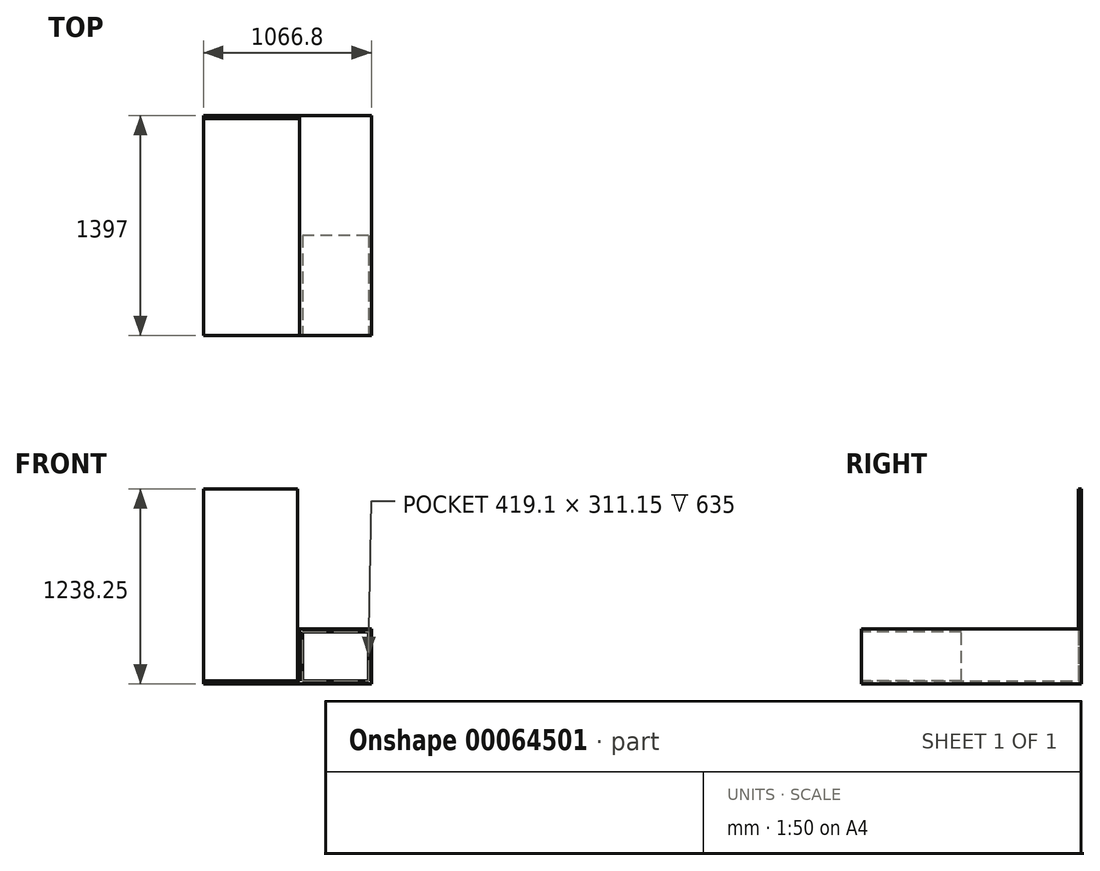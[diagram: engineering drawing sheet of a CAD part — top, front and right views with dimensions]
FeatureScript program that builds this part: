
annotation { "Feature Type Name" : "Feature", "Feature Type Description" : "" }
export const myFeature = defineFeature(function(context is Context, id is Id, definition is map)
    precondition{}
    {
        {
            var Q0;
            Q0=qCreatedBy(makeId("Top.planeOp"),FACE);
            var sketch = newSketch(context, id + "F0", { "sketchPlane" : qUnion([Q0])});
            skLineSegment(sketch, "E0.rect.bottom", {"start": v(533.4, -698.5) * mm, "end": v(-533.4, -698.5) * mm});
            skLineSegment(sketch, "E0.rect.top", {"start": v(533.4, 698.5) * mm, "end": v(-533.4, 698.5) * mm});
            skLineSegment(sketch, "E0.rect.left", {"start": v(533.4, -698.5) * mm, "end": v(533.4, 698.5) * mm});
            skLineSegment(sketch, "E0.rect.right", {"start": v(-533.4, -698.5) * mm, "end": v(-533.4, 698.5) * mm});
            skPoint(sketch, "E0.rect.middle", {"position": v(0, 0) * mm});
            skSolve(sketch);
        }
        {
            var Q0;
            Q0=makeQuery(id+"F0.imprint","IMPRINT",FACE,{"disambiguationData":[TD([[makeQuery(id+"F0.imprint","IMPRINT",EDGE,{"derivedFrom":sQuery(id+"F0.wireOp",EDGE,"E0.rect.bottom")}),-1.0]])]});
            extrude(context, id + "F1", {"entities" : qUnion([Q0]), "depth" : 19.05 * mm});
        }
        {
            var Q0;
            Q0=makeQuery(id+"F1.opExtrude","CAP_FACE",FACE,{"disambiguationData":[OSD([sQuery(id+"F0.wireOp",EDGE,"E0.rect.bottom"),sQuery(id+"F0.wireOp",EDGE,"E0.rect.top"),sQuery(id+"F0.wireOp",EDGE,"E0.rect.left"),sQuery(id+"F0.wireOp",EDGE,"E0.rect.right")])],"isStart":false});
            var sketch = newSketch(context, id + "F2", { "sketchPlane" : qUnion([Q0])});
            skLineSegment(sketch, "E1.bottom", {"start": v(533.4, -698.5) * mm, "end": v(76.2, -698.5) * mm});
            skLineSegment(sketch, "E1.top", {"start": v(533.4, 698.5) * mm, "end": v(76.2, 698.5) * mm});
            skLineSegment(sketch, "E1.left", {"start": v(533.4, -698.5) * mm, "end": v(533.4, 698.5) * mm});
            skLineSegment(sketch, "E1.right", {"start": v(76.2, -698.5) * mm, "end": v(76.2, 698.5) * mm});
            skSolve(sketch);
        }
        {
            var Q0;
            Q0=makeQuery(id+"F2.imprint","IMPRINT",FACE,{"disambiguationData":[TD([[makeQuery(id+"F2.imprint","IMPRINT",EDGE,{"derivedFrom":sQuery(id+"F2.wireOp",EDGE,"E1.bottom")}),-1.0]])]});
            extrude(context, id + "F3", {"entities" : qUnion([Q0]), "operationType" : NewBodyOperationType.ADD, "depth" : 330.2 * mm});
        }
        {
            var Q0;
            Q0=makeQuery(id+"F1.opExtrude","CAP_FACE",FACE,{"disambiguationData":[OSD([sQuery(id+"F0.wireOp",EDGE,"E0.rect.bottom"),sQuery(id+"F0.wireOp",EDGE,"E0.rect.top"),sQuery(id+"F0.wireOp",EDGE,"E0.rect.left"),sQuery(id+"F0.wireOp",EDGE,"E0.rect.right")])],"isStart":false});
            var sketch = newSketch(context, id + "F4", { "sketchPlane" : qUnion([Q0])});
            skLineSegment(sketch, "E2.bottom", {"start": v(-533.4, 698.5) * mm, "end": v(63.9, 698.5) * mm});
            skLineSegment(sketch, "E2.top", {"start": v(-533.4, 679.45) * mm, "end": v(63.9, 679.45) * mm});
            skLineSegment(sketch, "E2.left", {"start": v(-533.4, 698.5) * mm, "end": v(-533.4, 679.45) * mm});
            skLineSegment(sketch, "E2.right", {"start": v(63.9, 698.5) * mm, "end": v(63.9, 679.45) * mm});
            skSolve(sketch);
        }
        {
            var Q0;
            Q0 = qSketchRegion(id + "F4", true);
            extrude(context, id + "F5", {"entities" : qUnion([Q0]), "operationType" : NewBodyOperationType.ADD, "depth" : 1219.2 * mm});
        }
        {
            var Q0;
            Q0=makeQuery(id+"F3.boolean.opBoolean","MERGE",FACE,{"derivedFrom":[makeQuery(id+"F1.opExtrude","SWEPT_FACE",FACE,{"disambiguationData":[OSD([sQuery(id+"F0.wireOp",EDGE,"E0.rect.bottom")])]}),makeQuery(id+"F3.opExtrude","SWEPT_FACE",FACE,{"disambiguationData":[OSD([sQuery(id+"F2.wireOp",EDGE,"E1.bottom")])]})]});
            var sketch = newSketch(context, id + "F6", { "sketchPlane" : qUnion([Q0])});
            skLineSegment(sketch, "E3.rect.bottom", {"start": v(514.35, 19.05) * mm, "end": v(95.25, 19.05) * mm});
            skLineSegment(sketch, "E3.rect.top", {"start": v(514.35, 330.2) * mm, "end": v(95.25, 330.2) * mm});
            skLineSegment(sketch, "E3.rect.left", {"start": v(514.35, 19.05) * mm, "end": v(514.35, 330.2) * mm});
            skLineSegment(sketch, "E3.rect.right", {"start": v(95.25, 19.05) * mm, "end": v(95.25, 330.2) * mm});
            skPoint(sketch, "E3.rect.middle", {"position": v(304.8, 174.63) * mm});
            skSolve(sketch);
        }
        {
            var Q0;
            Q0 = qSketchRegion(id + "F6", true);
            extrude(context, id + "F7", {"entities" : qUnion([Q0]), "operationType" : NewBodyOperationType.REMOVE, "oppositeDirection" : true, "depth" : 635 * mm});
        }
    });
